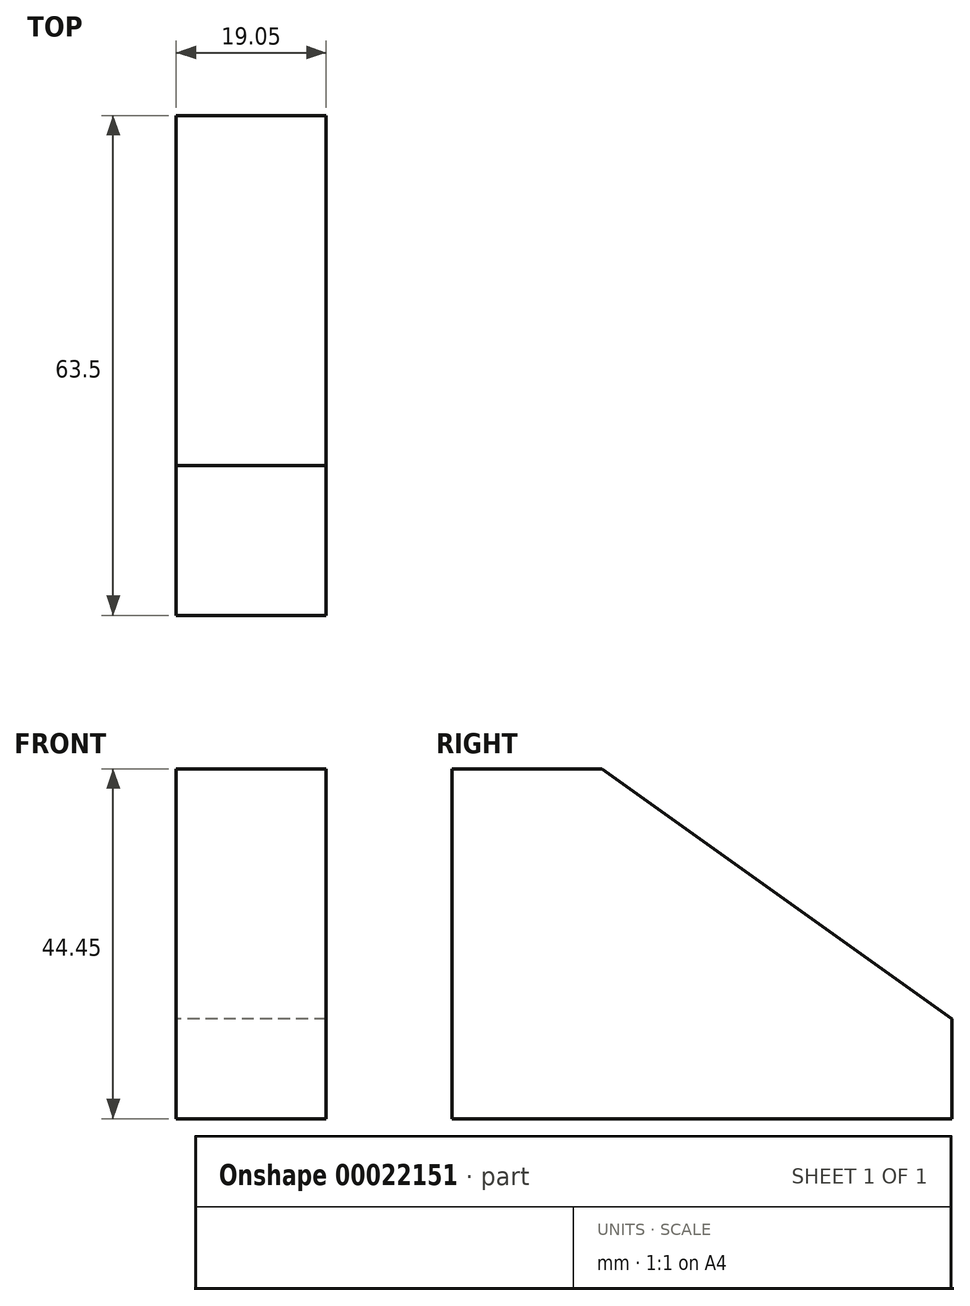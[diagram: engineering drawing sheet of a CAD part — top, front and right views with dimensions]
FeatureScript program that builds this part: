
annotation { "Feature Type Name" : "Feature", "Feature Type Description" : "" }
export const myFeature = defineFeature(function(context is Context, id is Id, definition is map)
    precondition{}
    {
        {
            var Q0;
            Q0=qCreatedBy(makeId("Right.planeOp"),FACE);
            var sketch = newSketch(context, id + "F0", { "sketchPlane" : qUnion([Q0])});
            skLineSegment(sketch, "E0", {"start": v(-47.99, 19.34) * mm, "end": v(-47.99, -25.11) * mm});
            skLineSegment(sketch, "E1", {"start": v(-47.99, -25.11) * mm, "end": v(15.51, -25.11) * mm});
            skLineSegment(sketch, "E2", {"start": v(15.51, -25.11) * mm, "end": v(15.51, -12.41) * mm});
            skLineSegment(sketch, "E3", {"start": v(15.51, -12.41) * mm, "end": v(-28.94, 19.34) * mm});
            skLineSegment(sketch, "E4", {"start": v(-28.94, 19.34) * mm, "end": v(-47.99, 19.34) * mm});
            skSolve(sketch);
        }
        {
            var Q0;
            Q0=makeQuery(id+"F0.imprint","IMPRINT",FACE,{"disambiguationData":[TD([[makeQuery(id+"F0.imprint","IMPRINT",EDGE,{"derivedFrom":sQuery(id+"F0.wireOp",EDGE,"E0")}),1.0]])]});
            extrude(context, id + "F1", {"entities" : qUnion([Q0]), "depth" : 19.05 * mm});
        }
    });
